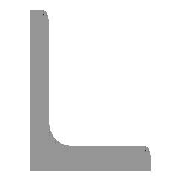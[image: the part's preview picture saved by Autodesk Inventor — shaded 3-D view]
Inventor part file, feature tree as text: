
AUTODESK INVENTOR PART (.ipt)
format: ipt  version: 2013 (Build 170138000, 138)  size: 129,024 bytes
history: native  units: mm (DEFAULTED — no unit token found)
features: other x4, plane x3, split x2, sketch x2
ambient origin geometry x8: Origin, YZ Plane, XZ Plane, XY Plane, X Axis, Y Axis, Z Axis, Center Point
bodies: Solid1 (feature_tree), Body (feature_tree)
feature tree (11):
  parser-record x1  (decoder bookkeeping rows leaked as tree rows — omitted from the tree; the rows remain in map.json)
  other  "Driven Length"
  other  "Start plane"
  other  "End plane"
  plane  "Work Plane4"
  split  "Split1"
  plane  "Work Plane5"
  split  "Split2"
  sketch  "Sketch3"  dims[d0=38.1mm]
  plane  "Work Plane3"
  sketch  "Sketch4"  dims[d1=38.1mm d2=4.7625mm d3=4.7625mm d4=1841.5mm d5=0.0mm d10=0.0mm d11=0.0mm d12=-0.0mm d13=1841.5mm d14=4.826mm d15=2.286mm d16=90.0deg d17=1841.5mm]
